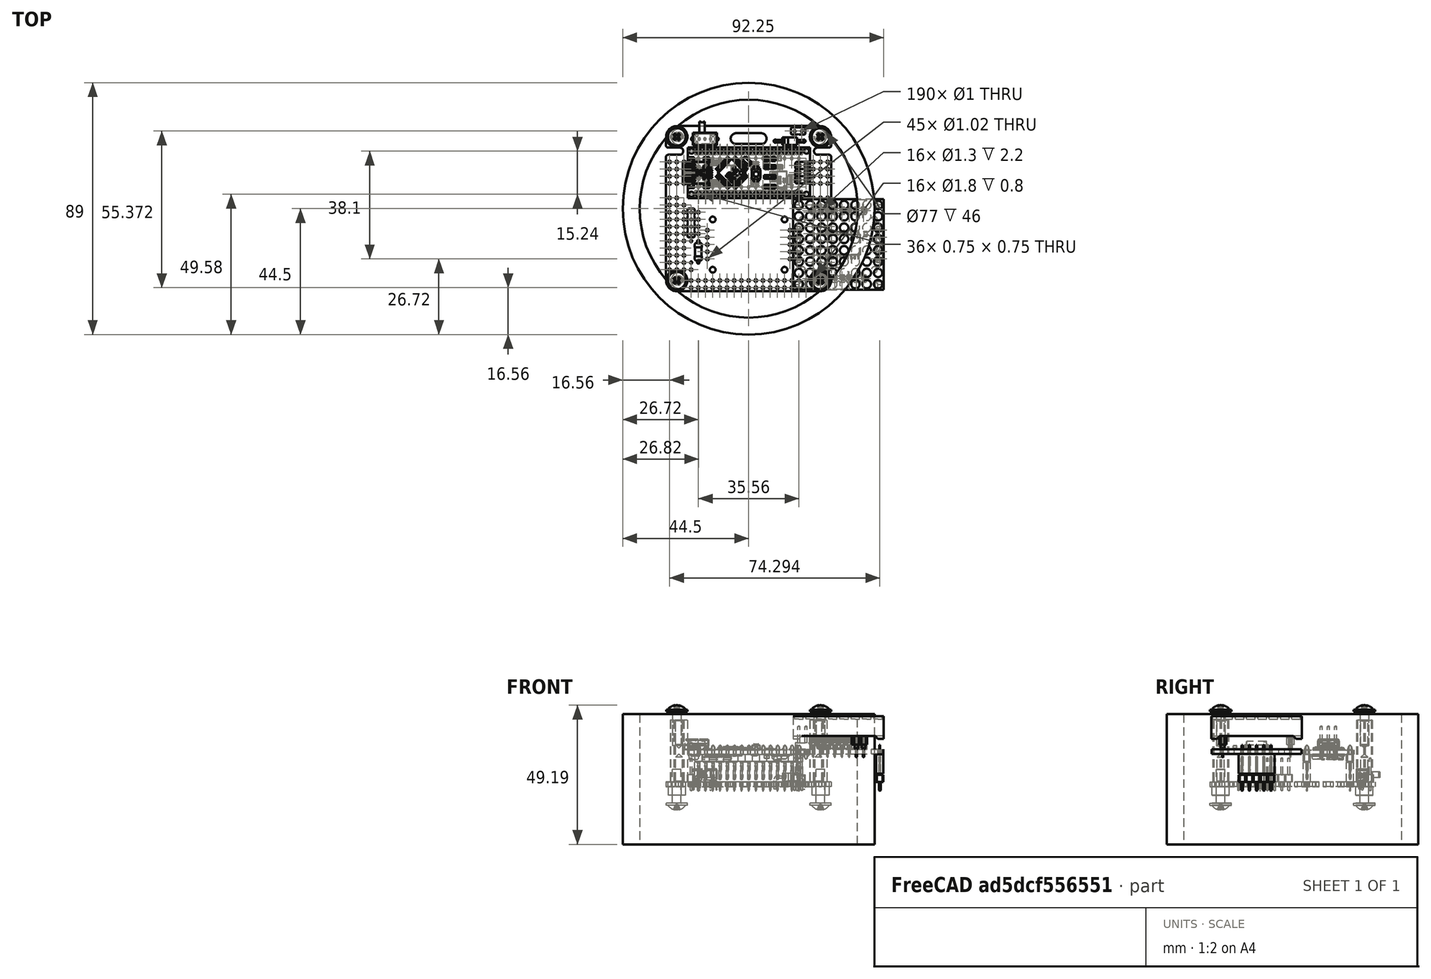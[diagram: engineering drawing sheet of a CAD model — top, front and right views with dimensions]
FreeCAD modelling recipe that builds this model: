
FCSTD DOCUMENT  (FreeCAD 2023.521R14555 (Git shallow))
Label: BagTag_v31
License: All rights reserved
LicenseURL: http://en.wikipedia.org/wiki/All_rights_reserved
objects: Part::Feature×22, Part::FeaturePython×12, App::DocumentObjectGroupPython×8, PartDesign::Body×7, Sketcher::SketchObject×5, PartDesign::SubShapeBinder×5, App::Part×5, PartDesign::Pad×4, App::DocumentObjectGroup×3, App::Link×3, Part::Part2DObjectPython×3, PartDesign::FeatureBase×3, PartDesign::CoordinateSystem×1, PartDesign::ShapeBinder×1, Part::SubShapeBinder×1
note: 80 computed .brp shape members not serialized (recipe doc carries the construction recipe); baked Part::Feature solids carry a one-line shape summary decoded from their .brp

FEATURE [Sketcher::SketchObject] Sketch
  ArcFitTolerance = 0
  AttachmentSupport = -> [XY_Plane011]
  ExternalBSplineMaxDegree = 0
  ExternalBSplineTolerance = 0
  FullyConstrained = true
  InternalTolerance = 1e-06
  InvalidShape = false
  MakeInternals = false
  MapMode = 5
  Support = -> [XY_Plane011]
  TreeRank = 0
  ValidateShape = false
  sketch-geometry (2):
    g0: Circle CenterX=0 CenterY=0 CenterZ=0 NormalX=0 NormalY=0 NormalZ=1 AngleXU=0 Radius=38.5
    g1: Circle CenterX=0 CenterY=0 CenterZ=0 NormalX=0 NormalY=0 NormalZ=1 AngleXU=0 Radius=44.5
  constraints (4):
    c: Coincident(g0,g-1)
    c: Diameter(g0) = 77
    c: Diameter(g1) = 89
    c: Coincident(g1,g0)
FEATURE [PartDesign::Pad] Pad
  AddSubType = 0
  AutoTaperInnerAngle = false
  CheckUpToFaceLimits = true
  ClaimChildren = false
  Direction = (0,0,1)
  Fit = 0
  FitJoin = 0
  InnerFit = 0
  InnerFitJoin = 0
  InvalidShape = false
  Length = 24
  Length2 = 22
  NewSolid = false
  Profile = -> Sketch
  Suppress = false
  TaperInnerAngle = 0
  TaperInnerAngleRev = 0
  TreeRank = 0
  Type = 4
  ValidateShape = true
  _ProfileBasedVersion = 0
FEATURE [PartDesign::Body] Body  label="PVC_pipe"
  AutoGroupSolids = false
  ClaimAllChildren = false
  ExportMode = 0
  Group = -> [Sketch,Pad]
  InvalidShape = false
  Origin = -> Origin011
  Tip = -> Pad
  TreeRank = 0
  ValidateShape = false
  _ExportChildren = -> [Pad]
  _GroupVersion = 1
FEATURE [Part::FeaturePython] Spacer  label="M3x22xx5.5-Spacer168"  # Fasteners workbench fastener (typed FeaturePython)
  InvalidShape = false
  Placement = pos=(-24.638,-25.4,0) rot=(0,0,1;0rad)
  TreeRank = 0
  ValidateShape = false
  diameter = 2
  invert = false
  leftHanded = false
  length = 17
  lengthCustom = 22
  matchOuter = false
  offset = 0
  thread = false
  type = 0
  width = 1
FEATURE [Part::FeaturePython] Spacer001  label="M3x22xx5.5-Spacer169"  # Fasteners workbench fastener (typed FeaturePython)
  InvalidShape = false
  Placement = pos=(24.638,-25.4,0) rot=(0,0,1;0rad)
  TreeRank = 0
  ValidateShape = false
  diameter = 2
  invert = false
  leftHanded = false
  length = 17
  lengthCustom = 22
  matchOuter = false
  offset = 0
  thread = false
  type = 0
  width = 1
FEATURE [Part::FeaturePython] Spacer002  label="M3x22xx5.5-Spacer"  # Fasteners workbench fastener (typed FeaturePython)
  InvalidShape = false
  Placement = pos=(-24.638,25.4,0) rot=(0,0,1;0rad)
  TreeRank = 0
  ValidateShape = false
  diameter = 2
  invert = false
  leftHanded = false
  length = 17
  lengthCustom = 22
  matchOuter = false
  offset = 0
  thread = false
  type = 0
  width = 1
FEATURE [Part::FeaturePython] Spacer003  label="M3x22xx5.5-Spacer170"  # Fasteners workbench fastener (typed FeaturePython)
  InvalidShape = false
  Placement = pos=(24.638,25.4,0) rot=(0,0,1;0rad)
  TreeRank = 0
  ValidateShape = false
  diameter = 2
  invert = false
  leftHanded = false
  length = 17
  lengthCustom = 22
  matchOuter = false
  offset = 0
  thread = false
  type = 0
  width = 1
FEATURE [Part::FeaturePython] Screw  label="M3x12-Screw"  # Fasteners workbench fastener (typed FeaturePython)
  InvalidShape = false
  Placement = pos=(-25.4,25.4,-7.5) rot=(-1,0,0;3.14159rad)
  TreeRank = 0
  ValidateShape = false
  baseObject = -> Body001 [Edge48]
  diameter = 1
  invert = true
  leftHanded = false
  length = 5
  lengthCustom = 12
  matchOuter = false
  offset = 0
  thread = false
  type = 22
FEATURE [Part::FeaturePython] Screw001  label="M3x12-Screw529"  # Fasteners workbench fastener (typed FeaturePython)
  InvalidShape = false
  Placement = pos=(25.4,25.4,-7.5) rot=(-1,0,0;3.14159rad)
  TreeRank = 0
  ValidateShape = false
  baseObject = -> Body001 [Edge45]
  diameter = 1
  invert = true
  leftHanded = false
  length = 5
  lengthCustom = 12
  matchOuter = false
  offset = 0
  thread = false
  type = 22
FEATURE [Part::FeaturePython] Screw002  label="M3x12-Screw530"  # Fasteners workbench fastener (typed FeaturePython)
  InvalidShape = false
  Placement = pos=(-25.4,-25.4,-7.5) rot=(-1,0,0;3.14159rad)
  TreeRank = 0
  ValidateShape = false
  baseObject = -> Body001 [Edge51]
  diameter = 1
  invert = true
  leftHanded = false
  length = 5
  lengthCustom = 12
  matchOuter = false
  offset = 0
  thread = false
  type = 22
FEATURE [Part::FeaturePython] Screw003  label="M3x12-Screw531"  # Fasteners workbench fastener (typed FeaturePython)
  InvalidShape = false
  Placement = pos=(25.4,-25.4,-7.5) rot=(-1,0,0;3.14159rad)
  TreeRank = 0
  ValidateShape = false
  baseObject = -> Body001 [Edge54]
  diameter = 1
  invert = true
  leftHanded = false
  length = 5
  lengthCustom = 12
  matchOuter = false
  offset = 0
  thread = false
  type = 22
FEATURE [PartDesign::SubShapeBinder] Binder003
  BindCopyOnChange = 0
  BindMode = 0
  ClaimChildren = false
  Context = -> Body003 [Binder003.]
  EdgeTolerance = 1e-06
  FillStyle = 0
  Fuse = false
  InvalidShape = false
  MakeFace = true
  MergeEdges = true
  OffsetFill = false
  OffsetIntersection = false
  OffsetJoinType = 0
  OffsetOpenResult = false
  Outline = false
  PartialLoad = false
  Relative = true
  SplitEdges = false
  Support = -> [Body001]
  TightBound = false
  TreeRank = 0
  ValidateShape = false
  _Version = 2
FEATURE [Part::FeaturePython] Screw004  label="M3x12-Screw692"  # Fasteners workbench fastener (typed FeaturePython)
  InvalidShape = false
  Placement = pos=(-25.4,25.4,24.9) rot=(0,0,1;0rad)
  TreeRank = 0
  ValidateShape = false
  baseObject = -> Body003 [Edge96]
  diameter = 1
  invert = false
  leftHanded = false
  length = 5
  lengthCustom = 12
  matchOuter = false
  offset = 0
  thread = false
  type = 22
FEATURE [Part::FeaturePython] Screw005  label="M3x12-Screw693"  # Fasteners workbench fastener (typed FeaturePython)
  InvalidShape = false
  Placement = pos=(25.4,25.4,24.9) rot=(0,0,1;0rad)
  TreeRank = 0
  ValidateShape = false
  baseObject = -> Body003 [Edge93]
  diameter = 1
  invert = false
  leftHanded = false
  length = 5
  lengthCustom = 12
  matchOuter = false
  offset = 0
  thread = false
  type = 22
FEATURE [Part::FeaturePython] Screw006  label="M3x12-Screw694"  # Fasteners workbench fastener (typed FeaturePython)
  InvalidShape = false
  Placement = pos=(-25.4,-25.4,24.9) rot=(0,0,1;0rad)
  TreeRank = 0
  ValidateShape = false
  baseObject = -> Body003 [Edge99]
  diameter = 1
  invert = false
  leftHanded = false
  length = 5
  lengthCustom = 12
  matchOuter = false
  offset = 0
  thread = false
  type = 22
FEATURE [Part::FeaturePython] Screw007  label="M3x12-Screw695"  # Fasteners workbench fastener (typed FeaturePython)
  InvalidShape = false
  Placement = pos=(25.4,-25.4,24.9) rot=(0,0,1;0rad)
  TreeRank = 0
  ValidateShape = false
  baseObject = -> Body003 [Edge102]
  diameter = 1
  invert = false
  leftHanded = false
  length = 5
  lengthCustom = 12
  matchOuter = false
  offset = 0
  thread = false
  type = 22
FEATURE [App::DocumentObjectGroup] Group001  label="Fasteners"
  ClaimAllChildren = true
  ExportMode = 1
  Group = -> [Spacer,Spacer001,Spacer002,Spacer003,Screw,Screw001,Screw002,Screw003,Screw004,Screw005,Screw006,Screw007]
  TreeRank = 0
  _GroupVersion = 1
FEATURE [PartDesign::SubShapeBinder] Binder005  label="Binder005(M3x22xx5.5-Spacer033)"
  BindCopyOnChange = 0
  BindMode = 0
  ClaimChildren = false
  Context = -> Body003 [Binder005.]
  EdgeTolerance = 1e-06
  FillStyle = 0
  Fuse = false
  InvalidShape = false
  MakeFace = true
  MergeEdges = true
  OffsetFill = false
  OffsetIntersection = false
  OffsetJoinType = 0
  OffsetOpenResult = false
  Outline = false
  PartialLoad = false
  Relative = true
  SplitEdges = false
  Support = -> [Spacer]
  TightBound = false
  TreeRank = 1
  ValidateShape = false
  _Version = 8
FEATURE [Part::Feature] Compound  label="pp3_battery"
  InvalidShape = false
  Placement = pos=(2.6,-25,8.6) rot=(1,0,0;1.5708rad)
  TreeRank = 36
  ValidateShape = false
  shape: bbox 46.52 x 16.6 x 26 mm, 243 faces, 0 solids (baked)
FEATURE [Part::Feature] trajectory_line
  InvalidShape = false
  TreeRank = 545
  ValidateShape = false
  shape: bbox 49.28 x 50.8 x 150 mm, 0 faces, 0 solids (baked)
FEATURE [App::DocumentObjectGroupPython] BoltGroup  # scripted group (container) (typed FeaturePython)
  AnimationStepTime = 0.1
  AnimationSteps = 20
  ClaimAllChildren = true
  Distance = 150
  ExportMode = 0
  Group = -> [trajectory_line]
  Revolutions = 0
  TreeRank = 5
  _GroupVersion = 1
FEATURE [Part::Feature] trajectory_line001
  InvalidShape = false
  TreeRank = 546
  ValidateShape = false
  shape: bbox 2e-07 x 2e-07 x 140 mm, 0 faces, 0 solids (baked)
FEATURE [App::DocumentObjectGroupPython] SimpleGroup  # scripted group (container) (typed FeaturePython)
  AnimationStepTime = 0.05
  AnimationSteps = 20
  ClaimAllChildren = true
  Distance = 140
  ExportMode = 0
  Group = -> [trajectory_line001]
  Revolutions = 0
  TreeRank = 9
  _GroupVersion = 1
FEATURE [Part::Feature] trajectory_line002
  InvalidShape = false
  TreeRank = 547
  ValidateShape = false
  shape: bbox 49.28 x 50.8 x 120 mm, 0 faces, 0 solids (baked)
FEATURE [App::DocumentObjectGroupPython] BoltGroup001  # scripted group (container) (typed FeaturePython)
  AnimationStepTime = 0.05
  AnimationSteps = 20
  ClaimAllChildren = true
  Distance = 120
  ExportMode = 0
  Group = -> [trajectory_line002]
  Revolutions = 0
  TreeRank = 15
  _GroupVersion = 1
FEATURE [Part::Feature] trajectory_line003
  InvalidShape = false
  TreeRank = 548
  ValidateShape = false
  shape: bbox 2e-07 x 100 x 2e-07 mm, 0 faces, 0 solids (baked)
FEATURE [App::DocumentObjectGroupPython] SimpleGroup001  # scripted group (container) (typed FeaturePython)
  AnimationStepTime = 0
  AnimationSteps = 20
  ClaimAllChildren = true
  Distance = 100
  ExportMode = 0
  Group = -> [trajectory_line003]
  Revolutions = 0
  TreeRank = 42
  _GroupVersion = 1
FEATURE [Part::Feature] trajectory_line004
  InvalidShape = false
  TreeRank = 549
  ValidateShape = false
  shape: bbox 2e-07 x 2e-07 x 100 mm, 0 faces, 0 solids (baked)
FEATURE [App::DocumentObjectGroupPython] SimpleGroup002  # scripted group (container) (typed FeaturePython)
  AnimationStepTime = 0
  AnimationSteps = 20
  ClaimAllChildren = true
  Distance = 100
  ExportMode = 0
  Group = -> [trajectory_line004]
  Revolutions = 0
  TreeRank = 518
  _GroupVersion = 1
FEATURE [Part::Feature] trajectory_line005
  InvalidShape = false
  TreeRank = 550
  ValidateShape = false
  shape: bbox 2e-07 x 2e-07 x 80 mm, 0 faces, 0 solids (baked)
FEATURE [App::DocumentObjectGroupPython] BoltGroup002  # scripted group (container) (typed FeaturePython)
  AnimationStepTime = 0
  AnimationSteps = 20
  ClaimAllChildren = true
  Distance = 80
  ExportMode = 0
  Group = -> [trajectory_line005]
  Revolutions = 0
  TreeRank = 530
  _GroupVersion = 1
FEATURE [Part::Feature] trajectory_line006
  InvalidShape = false
  TreeRank = 543
  ValidateShape = false
  shape: bbox 2e-07 x 2e-07 x 20 mm, 0 faces, 0 solids (baked)
FEATURE [App::DocumentObjectGroupPython] SimpleGroup003  # scripted group (container) (typed FeaturePython)
  AnimationStepTime = 0
  AnimationSteps = 20
  ClaimAllChildren = true
  Distance = 50
  ExportMode = 0
  Group = -> [trajectory_line006]
  Revolutions = 0
  TreeRank = 544
  _GroupVersion = 1
FEATURE [App::DocumentObjectGroupPython] ExplodedAssembly  # scripted group (container) (typed FeaturePython)
  AnimationStep = 0
  ClaimAllChildren = true
  CurrentTrajectory = 0
  ExportMode = 0
  Group = -> [BoltGroup,SimpleGroup,BoltGroup001,SimpleGroup001,SimpleGroup002,BoltGroup002,SimpleGroup003]
  InAnimation = false
  RemoveAllTrajectories = false
  ResetAnimation = false
  TreeRank = 2
  _GroupVersion = 1
FEATURE [PartDesign::CoordinateSystem] Local_CS_fc76
  AttacherType = Attacher::AttachEngine3D
  FixShape = 1
  InvalidShape = false
  MapMode = 2
  TreeRank = 596
  ValidateShape = false
FEATURE [Part::Feature] Pcb_fc76
  FixShape = 1
  InvalidShape = false
  Placement = pos=(-80.01,80.01,0) rot=(0,0,1;0rad)
  TreeRank = 597
  ValidateShape = false
  shape: bbox 58.42 x 58.42 x 1.6 mm, 260 faces (baked)
FEATURE [Sketcher::SketchObject] PCB_Sketch_fc76
  ArcFitTolerance = 1e-06
  ExternalBSplineMaxDegree = 5
  ExternalBSplineTolerance = 0.0001
  FixShape = 1
  FullyConstrained = false
  InternalTolerance = 1e-06
  InvalidShape = false
  MakeInternals = false
  TreeRank = 602
  ValidateShape = false
  sketch-geometry (28):
    g0: LineSegment StartX=4.445 StartY=22.86 StartZ=0 EndX=-4.445 EndY=22.86 EndZ=0
    g1: LineSegment StartX=28.448 StartY=21.59 StartZ=0 EndX=24.384 EndY=21.59 EndZ=0
    g2: LineSegment StartX=-29.21 StartY=25.781 StartZ=0 EndX=-25.781 EndY=29.21 EndZ=0
    g3: LineSegment StartX=-25.781 StartY=29.21 StartZ=0 EndX=25.781 EndY=29.21 EndZ=0
    g4: LineSegment StartX=29.21 StartY=25.781 StartZ=0 EndX=25.781 EndY=29.21 EndZ=0
    g5: LineSegment StartX=25.781 StartY=-29.21 StartZ=0 EndX=29.21 EndY=-25.781 EndZ=0
    g6: LineSegment StartX=25.781 StartY=-29.21 StartZ=0 EndX=-25.781 EndY=-29.21 EndZ=0
    g7: LineSegment StartX=-29.21 StartY=-25.781 StartZ=0 EndX=-25.781 EndY=-29.21 EndZ=0
    g8: LineSegment StartX=29.21 StartY=25.781 StartZ=0 EndX=29.21 EndY=22.352 EndZ=0
    g9: LineSegment StartX=29.21 StartY=18.288 StartZ=0 EndX=29.21 EndY=-25.781 EndZ=0
    g10: LineSegment StartX=-24.384 StartY=21.59 StartZ=0 EndX=-28.448 EndY=21.59 EndZ=0
    g11: LineSegment StartX=-28.448 StartY=19.05 StartZ=0 EndX=-24.384 EndY=19.05 EndZ=0
    g12: LineSegment StartX=-4.445 StartY=26.67 StartZ=0 EndX=4.445 EndY=26.67 EndZ=0
    g13: LineSegment StartX=24.384 StartY=19.05 StartZ=0 EndX=28.448 EndY=19.05 EndZ=0
    g14: LineSegment StartX=-29.21 StartY=25.781 StartZ=0 EndX=-29.21 EndY=22.352 EndZ=0
    g15: LineSegment StartX=-29.21 StartY=-25.781 StartZ=0 EndX=-29.21 EndY=18.288 EndZ=0
    g16: ArcOfCircle CenterX=28.448 CenterY=18.288 CenterZ=0 NormalX=0 NormalY=0 NormalZ=-1 AngleXU=1.5708 Radius=0.762001 StartAngle=0 EndAngle=1.57079
    g17: ArcOfCircle CenterX=-4.445 CenterY=24.765 CenterZ=0 NormalX=0 NormalY=0 NormalZ=-1 AngleXU=-1.5708 Radius=1.905 StartAngle=0 EndAngle=3.14159
    g18: ArcOfCircle CenterX=-28.448 CenterY=18.288 CenterZ=0 NormalX=0 NormalY=0 NormalZ=-1 AngleXU=1.64556e-06 Radius=0.762001 StartAngle=0 EndAngle=1.57079
    g19: ArcOfCircle CenterX=-28.448 CenterY=22.352 CenterZ=0 NormalX=0 NormalY=0 NormalZ=-1 AngleXU=-1.57079 Radius=0.762001 StartAngle=0 EndAngle=1.57079
    g20: ArcOfCircle CenterX=-24.384 CenterY=20.32 CenterZ=0 NormalX=0 NormalY=0 NormalZ=-1 AngleXU=1.5708 Radius=1.27 StartAngle=0 EndAngle=3.14159
    g21: ArcOfCircle CenterX=4.445 CenterY=24.765 CenterZ=0 NormalX=0 NormalY=0 NormalZ=-1 AngleXU=1.5708 Radius=1.905 StartAngle=0 EndAngle=3.14159
    g22: ArcOfCircle CenterX=24.384 CenterY=20.32 CenterZ=0 NormalX=0 NormalY=0 NormalZ=-1 AngleXU=-1.5708 Radius=1.27 StartAngle=0 EndAngle=3.14159
    g23: ArcOfCircle CenterX=28.448 CenterY=22.352 CenterZ=0 NormalX=0 NormalY=0 NormalZ=-1 AngleXU=-3.14159 Radius=0.762001 StartAngle=0 EndAngle=1.57079
    g24: Circle CenterX=25.4 CenterY=25.4 CenterZ=0 NormalX=0 NormalY=0 NormalZ=1 AngleXU=0 Radius=1.524
    g25: Circle CenterX=-25.4 CenterY=-25.4 CenterZ=0 NormalX=0 NormalY=0 NormalZ=1 AngleXU=0 Radius=1.524
    g26: Circle CenterX=25.4 CenterY=-25.4 CenterZ=0 NormalX=0 NormalY=0 NormalZ=1 AngleXU=0 Radius=1.524
    g27: Circle CenterX=-25.4 CenterY=25.4 CenterZ=0 NormalX=0 NormalY=0 NormalZ=1 AngleXU=0 Radius=1.524
  constraints (24):
    c: Coincident(g7,g15)
    c: Coincident(g15,g18)
    c: Coincident(g14,g19)
    c: Coincident(g2,g14)
    c: Coincident(g11,g18)
    c: Coincident(g10,g19)
    c: Coincident(g6,g7)
    c: Coincident(g2,g3)
    c: Coincident(g11,g20)
    c: Coincident(g10,g20)
    c: Coincident(g0,g17)
    c: Coincident(g12,g17)
    c: Coincident(g0,g21)
    c: Coincident(g12,g21)
    c: Coincident(g13,g22)
    c: Coincident(g1,g22)
    c: Coincident(g5,g6)
    c: Coincident(g3,g4)
    c: Coincident(g13,g16)
    c: Coincident(g1,g23)
    c: Coincident(g5,g9)
    c: Coincident(g9,g16)
    c: Coincident(g8,g23)
    c: Coincident(g4,g8)
FEATURE [App::Part] Bot_fc76
  ClaimAllChildren = false
  ExportMode = 1
  Origin = -> Origin028
  TreeRank = 608
  _GroupVersion = 1
FEATURE [Part::Feature] Shape001  label="LED2_FC_16_cp_sp_3f0951532924"
  FixShape = 1
  InvalidShape = false
  Placement = pos=(31.75,-12.7,0) rot=(0,0,1;0rad)
  TreeRank = 685
  ValidateShape = false
  shape: bbox 32 x 32 x 26.3 mm, 2206 faces, 44 solids (baked)
FEATURE [Part::Feature] Shape002  label="BT1_PinHeader_1x02_P254mm_Vertical_64228b7c207f"
  FixShape = 1
  InvalidShape = false
  Placement = pos=(16.246,27.432,0) rot=(0,0,1;1.5708rad)
  TreeRank = 705
  ValidateShape = false
  shape: bbox 5.08 x 2.54 x 11.54 mm, 52 faces (baked)
FEATURE [Part::Feature] Shape004  label="J2_PinHeader_1x04_P254mm_Vertical_b8c18ff84878"
  FixShape = 1
  InvalidShape = false
  Placement = pos=(-20.32,-1.27,0) rot=(0,0,1;0rad)
  TreeRank = 733
  ValidateShape = false
  shape: bbox 2.54 x 10.16 x 11.54 mm, 100 faces (baked)
FEATURE [App::Link] LED2_FC_16_cp_sp_3f0951532924_ln_  label="LED1_FC_16_cp_sp_494d2cd2c793"
  AutoLinkLabel = true
  AutoPlacement = true
  LinkPlacement = pos=(0,-12.7,0) rot=(0,0,1;0rad)
  LinkedObject = -> Shape001
  Placement = pos=(0,-12.7,0) rot=(0,0,1;0rad)
  SyncGroupVisibility = false
  TreeRank = 735
  _LinkVersion = 1
FEATURE [App::Link] J2_PinHeader_1x04_P254mm_Vertical_b8c18ff84878_ln_  label="J1_PinHeader_1x04_P254mm_Vertical_d596b9d5dcda"
  AutoLinkLabel = true
  AutoPlacement = true
  LinkPlacement = pos=(-17.78,-1.27,0) rot=(0,0,1;0rad)
  LinkedObject = -> Shape004
  Placement = pos=(-17.78,-1.27,0) rot=(0,0,1;0rad)
  SyncGroupVisibility = false
  TreeRank = 761
  _LinkVersion = 1
FEATURE [Part::Feature] Shape005  label="R2_R_Axial_DIN0207_L63mm_D25mm_P762mm_Horizontal_4ffd937b06bc"
  FixShape = 1
  InvalidShape = false
  Placement = pos=(-17.78,-19.05,0) rot=(0,0,1;1.5708rad)
  TreeRank = 805
  ValidateShape = false
  shape: bbox 2.706 x 8.418 x 5.603 mm, 15 faces (baked)
FEATURE [Part::Feature] Shape006  label="U1_arduino_nano_socket_d5ff97aaa247"
  FixShape = 1
  InvalidShape = false
  Placement = pos=(20.32,12.7,0) rot=(0,0,-1;1.5708rad)
  TreeRank = 837
  ValidateShape = false
  shape: bbox 45 x 18 x 22.97 mm, 7207 faces, 57 solids (baked)
FEATURE [Part::Feature] Shape007  label="SW1_1_219a87e7a09f"
  FixShape = 1
  InvalidShape = false
  Placement = pos=(-13.462,24.638,0) rot=(0,0,1;3.14159rad)
  TreeRank = 855
  ValidateShape = false
  shape: bbox 8.6 x 8.4 x 7.6 mm, 200 faces (baked)
FEATURE [Part::Feature] Shape008  label="D1_D_DO-41_SOD81_P10.16mm_Horizontal_32ec51f60e8f"
  FixShape = 1
  InvalidShape = false
  Placement = pos=(9.398,23.876,0) rot=(0,0,1;0rad)
  TreeRank = 892
  ValidateShape = false
  shape: bbox 11.16 x 2.72 x 5.71 mm, 15 faces (baked)
FEATURE [App::Link] R2_R_Axial_DIN0207_L63mm_D25mm_P762mm_Horizontal_4ffd937b06bc_ln_  label="R1_R_Axial_DIN0207_L63mm_D25mm_P762mm_Horizontal_6afa1d7f9f45"
  AutoLinkLabel = true
  AutoPlacement = true
  LinkPlacement = pos=(-20.32,-19.05,0) rot=(0,0,1;1.5708rad)
  LinkedObject = -> Shape005
  Placement = pos=(-20.32,-19.05,0) rot=(0,0,1;1.5708rad)
  SyncGroupVisibility = false
  TreeRank = 894
  _LinkVersion = 1
FEATURE [App::Part] Top_fc76
  ClaimAllChildren = false
  ExportMode = 1
  Group = -> [Shape001,Shape002,Shape004,LED2_FC_16_cp_sp_3f0951532924_ln_,J2_PinHeader_1x04_P254mm_Vertical_b8c18ff84878_ln_,Shape005,Shape006,Shape007,Shape008,R2_R_Axial_DIN0207_L63mm_D25mm_P762mm_Horizontal_4ffd937b06bc_ln_]
  Origin = -> Origin027
  TreeRank = 606
  _ExportChildren = -> [Shape001,Shape002,Shape004,LED2_FC_16_cp_sp_3f0951532924_ln_,J2_PinHeader_1x04_P254mm_Vertical_b8c18ff84878_ln_,Shape005,Shape006,Shape007,Shape008,R2_R_Axial_DIN0207_L63mm_D25mm_P762mm_Horizontal_4ffd937b06bc_ln_]
  _GroupVersion = 1
FEATURE [App::Part] Step_Models_fc76
  ClaimAllChildren = false
  ExportMode = 1
  Group = -> [Top_fc76,Bot_fc76]
  Origin = -> Origin026
  TreeRank = 604
  _ExportChildren = -> [Top_fc76,Bot_fc76]
  _GroupVersion = 1
FEATURE [Part::Feature] pads_area001  label="topPads_fc76"
  FixShape = 1
  InvalidShape = false
  Placement = pos=(-80.01,80.01,0.02) rot=(0,0,1;0rad)
  TreeRank = 2449
  ValidateShape = false
  shape: bbox 57.58 x 57.07 x 2e-07 mm, 226 faces, 0 solids (baked)
FEATURE [Part::Feature] Shape009  label="topTracks_fc76"
  FixShape = 1
  InvalidShape = false
  Placement = pos=(-80.01,80.01,0.01) rot=(0,0,1;0rad)
  TreeRank = 2479
  ValidateShape = false
  shape: bbox 50.8 x 47.75 x 2e-07 mm, 60 faces, 0 solids (baked)
FEATURE [Part::Feature] pads_area002001  label="botPads_fc76"
  FixShape = 1
  InvalidShape = false
  Placement = pos=(-80.01,80.01,-1.62) rot=(0,0,1;0rad)
  TreeRank = 3882
  ValidateShape = false
  shape: bbox 57.58 x 57.07 x 2e-07 mm, 226 faces, 0 solids (baked)
FEATURE [Part::Feature] Shape010001  label="botTracks_fc76"
  FixShape = 1
  InvalidShape = false
  Placement = pos=(-80.01,80.01,-1.61) rot=(0,0,1;0rad)
  TreeRank = 3912
  ValidateShape = false
  shape: bbox 49.91 x 45.04 x 2e-07 mm, 36 faces, 0 solids (baked)
FEATURE [Part::Feature] zones_area001  label="botZones_fc76"
  FixShape = 1
  InvalidShape = false
  Placement = pos=(-80.01,80.01,-1.61) rot=(0,0,1;0rad)
  TreeRank = 4046
  ValidateShape = false
  shape: bbox 58.47 x 58.47 x 2e-07 mm, 21 faces, 0 solids (baked)
FEATURE [Part::Feature] topSilks_ac4f
  FixShape = 1
  InvalidShape = false
  Placement = pos=(-80.01,80.01,0.07) rot=(0,0,1;0rad)
  TreeRank = 4416
  ValidateShape = false
  shape: bbox 58.06 x 57.85 x 2e-07 mm, 363 faces, 0 solids (baked)
FEATURE [App::Part] Board_Geoms_fc76
  ClaimAllChildren = false
  ExportMode = 1
  Group = -> [Pcb_fc76,PCB_Sketch_fc76,pads_area001,Shape009,pads_area002001,Shape010001,zones_area001,topSilks_ac4f]
  Origin = -> Origin
  TreeRank = 599
  _ExportChildren = -> [Pcb_fc76,PCB_Sketch_fc76,pads_area001,Shape009,pads_area002001,Shape010001,zones_area001,topSilks_ac4f]
  _GroupVersion = 1
FEATURE [App::Part] Board_fc76  label="BagTag"
  ClaimAllChildren = false
  ExportMode = 1
  Group = -> [Local_CS_fc76,Board_Geoms_fc76,Step_Models_fc76]
  Origin = -> Origin025
  TreeRank = 601
  _ExportChildren = -> [Local_CS_fc76,Board_Geoms_fc76,Step_Models_fc76]
  _GroupVersion = 1
FEATURE [PartDesign::ShapeBinder] ShapeBinder
  FixShape = 1
  InvalidShape = false
  Placement = pos=(-80.01,80.01,0) rot=(0,0,1;0rad)
  Support = -> [Pcb_fc76]
  TraceSupport = false
  TreeRank = 4417
  ValidateShape = false
FEATURE [Part::SubShapeBinder] Import  label="Import(Pcb_fc76)"
  BindCopyOnChange = 0
  BindMode = 0
  ClaimChildren = false
  Context = -> Body001 [Import.]
  EdgeTolerance = 1e-06
  FillStyle = 0
  FixShape = 1
  Fuse = false
  InvalidShape = false
  MakeFace = false
  MergeEdges = true
  OffsetFill = false
  OffsetIntersection = false
  OffsetJoinType = 0
  OffsetOpenResult = false
  Outline = false
  PartialLoad = false
  Relative = true
  SplitEdges = false
  Support = -> [Board_fc76[Board_Geoms_fc76.Pcb_fc76.]]
  TightBound = false
  TreeRank = 4418
  ValidateShape = false
  _Version = 8
FEATURE [Sketcher::SketchObject] Sketch001
  ArcFitTolerance = 0
  AttachmentSupport = -> [XY_Plane020]
  ExternalBSplineMaxDegree = 0
  ExternalBSplineTolerance = 0
  ExternalGeometry = -> [Import]
  FullyConstrained = true
  InternalTolerance = 1e-06
  InvalidShape = false
  MakeInternals = false
  MapMode = 5
  Support = -> [XY_Plane020]
  TreeRank = 0
  ValidateShape = false
  sketch-geometry (22):
    g0: LineSegment StartX=-25.4 StartY=29.9 StartZ=0 EndX=25.4 EndY=29.9 EndZ=0
    g1: LineSegment StartX=29.9 StartY=25.4 StartZ=0 EndX=29.9 EndY=-41.6 EndZ=0
    g2: LineSegment StartX=25.4 StartY=-46.1 StartZ=0 EndX=-25.4 EndY=-46.1 EndZ=0
    g3: LineSegment StartX=-29.9 StartY=-41.6 StartZ=0 EndX=-29.9 EndY=25.4 EndZ=0
    g4: ArcOfCircle CenterX=-25.4 CenterY=25.4 CenterZ=0 NormalX=0 NormalY=0 NormalZ=1 AngleXU=0 Radius=4.5 StartAngle=1.5708 EndAngle=3.14159
    g5: GeomPoint [constr] X=-29.9 Y=29.9 Z=0
    g6: ArcOfCircle CenterX=25.4 CenterY=25.4 CenterZ=0 NormalX=0 NormalY=0 NormalZ=1 AngleXU=0 Radius=4.5 StartAngle=0 EndAngle=1.5708
    g7: GeomPoint [constr] X=29.9 Y=29.9 Z=0
    g8: ArcOfCircle CenterX=25.4 CenterY=-41.6 CenterZ=0 NormalX=0 NormalY=0 NormalZ=1 AngleXU=0 Radius=4.5 StartAngle=4.71239 EndAngle=6.28319
    g9: GeomPoint [constr] X=29.9 Y=-46.1 Z=0
    g10: ArcOfCircle CenterX=-25.4 CenterY=-41.6 CenterZ=0 NormalX=0 NormalY=0 NormalZ=1 AngleXU=0 Radius=4.5 StartAngle=3.14159 EndAngle=4.71239
    g11: GeomPoint [constr] X=-29.9 Y=-46.1 Z=0
    g12: Circle CenterX=-25.4 CenterY=-41.6 CenterZ=0 NormalX=0 NormalY=0 NormalZ=1 AngleXU=0 Radius=1.525
    g13: Circle CenterX=25.4 CenterY=-41.6 CenterZ=0 NormalX=0 NormalY=0 NormalZ=1 AngleXU=0 Radius=1.525
    g14: Circle CenterX=25.4 CenterY=25.4 CenterZ=0 NormalX=0 NormalY=0 NormalZ=1 AngleXU=0 Radius=1.525
    g15: Circle CenterX=-25.4 CenterY=25.4 CenterZ=0 NormalX=0 NormalY=0 NormalZ=1 AngleXU=0 Radius=1.525
    g16: ArcOfCircle CenterX=-4.445 CenterY=24.765 CenterZ=0 NormalX=0 NormalY=0 NormalZ=1 AngleXU=0 Radius=1.905 StartAngle=1.5708 EndAngle=4.71239
    g17: ArcOfCircle CenterX=4.445 CenterY=24.765 CenterZ=0 NormalX=0 NormalY=0 NormalZ=1 AngleXU=0 Radius=1.905 StartAngle=4.71239 EndAngle=7.85398
    g18: LineSegment StartX=-4.445 StartY=22.86 StartZ=0 EndX=4.445 EndY=22.86 EndZ=0
    g19: LineSegment StartX=-4.445 StartY=26.67 StartZ=0 EndX=4.445 EndY=26.67 EndZ=0
    g20: Circle CenterX=-25.4 CenterY=-25.4 CenterZ=0 NormalX=0 NormalY=0 NormalZ=1 AngleXU=0 Radius=1.525
    g21: Circle CenterX=25.4 CenterY=-25.4 CenterZ=0 NormalX=0 NormalY=0 NormalZ=1 AngleXU=0 Radius=1.525
  constraints (46):
    c: Horizontal(g0)
    c: Horizontal(g2)
    c: Vertical(g1)
    c: Vertical(g3)
    c: PointOnObject(g5,g0)
    c: PointOnObject(g5,g3)
    c: Tangent(g0,g4) = 1.5708
    c: Tangent(g3,g4) = 1.5708
    c: PointOnObject(g7,g0)
    c: PointOnObject(g7,g1)
    c: Tangent(g0,g6) = 1.5708
    c: Tangent(g1,g6) = 1.5708
    c: PointOnObject(g9,g1)
    c: PointOnObject(g9,g2)
    c: Tangent(g1,g8) = 1.5708
    c: Tangent(g2,g8) = 1.5708
    c: PointOnObject(g11,g3)
    c: PointOnObject(g11,g2)
    c: Tangent(g3,g10) = 1.5708
    c: Tangent(g2,g10) = 1.5708
    c: Equal(g10,g8)
    c: Equal(g8,g6)
    c: Coincident(g12,g10)
    c: Coincident(g13,g8)
    c: Coincident(g14,g6)
    c: Coincident(g15,g4)
    c: Equal(g15,g14)
    c: Equal(g14,g13)
    c: Equal(g13,g12)
    c: Tangent(g16,g19) = 1.5708
    c: Tangent(g16,g18) = -1.5708
    c: Tangent(g18,g17) = -1.5708
    c: Tangent(g19,g17) = 1.5708
    c: Horizontal(g18)
    c: Equal(g20,g15)
    c: Diameter(g15) = 3.05
    c: Equal(g21,g15)
    c: DistanceY(g2,g0) = 76
    c: Coincident(g16,g-7)
    c: Coincident(g17,g-8)
    c: Equal(g17,g-8)
    c: Coincident(g4,g-3)
    c: Coincident(g6,g-4)
    c: Coincident(g20,g-6)
    c: Coincident(g21,g-5)
    c: Radius(g4) = 4.5
FEATURE [PartDesign::Pad] Pad001
  AddSubType = 0
  AutoTaperInnerAngle = false
  CheckUpToFaceLimits = true
  ClaimChildren = false
  Direction = (0,0,1)
  Fit = 0
  FitJoin = 0
  InnerFit = 0
  InnerFitJoin = 0
  InvalidShape = false
  Length = 3
  Length2 = 100
  NewSolid = false
  Profile = -> Sketch001
  Reversed = true
  Suppress = false
  TaperInnerAngle = 0
  TaperInnerAngleRev = 0
  TreeRank = 0
  Type = 0
  ValidateShape = true
  _ProfileBasedVersion = 0
FEATURE [PartDesign::Body] Body001  label="Plate_bottom"
  AutoGroupSolids = false
  ClaimAllChildren = false
  ExportMode = 0
  Group = -> [Sketch001,Pad001,ShapeBinder,Import]
  InvalidShape = false
  Origin = -> Origin020
  Placement = pos=(0,0,-4.5) rot=(0,0,1;0rad)
  Tip = -> Pad001
  TreeRank = 0
  ValidateShape = false
  _ExportChildren = -> [Pad001,ShapeBinder,Import]
  _GroupVersion = 1
FEATURE [Part::Part2DObjectPython] Shape2DView  # Draft 2D object (typed FeaturePython)
  AutoUpdate = true
  Base = -> Body001
  Clip = false
  FuseArch = false
  HiddenLines = false
  InPlace = true
  InvalidShape = false
  OnlySolids = false
  Projection = (0,0,1)
  ProjectionMode = 0
  SegmentLength = 0.05
  Tessellation = false
  TreeRank = 551
  ValidateShape = false
  VisibleOnly = false
FEATURE [PartDesign::SubShapeBinder] Binder006  label="Binder006(LED1_FC_16_cp_sp_494d2cd2c793)"
  BindCopyOnChange = 0
  BindMode = 0
  ClaimChildren = false
  Context = -> Body003 [Binder006.]
  EdgeTolerance = 1e-06
  FillStyle = 0
  FixShape = 1
  Fuse = false
  InvalidShape = false
  MakeFace = true
  MergeEdges = true
  OffsetFill = false
  OffsetIntersection = false
  OffsetJoinType = 0
  OffsetOpenResult = false
  Outline = false
  PartialLoad = false
  Relative = true
  SplitEdges = false
  Support = -> [Board_fc76[Step_Models_fc76.Top_fc76.LED2_FC_16_cp_sp_3f0951532924_ln_.]]
  TightBound = false
  TreeRank = 4419
  ValidateShape = false
  _Version = 8
FEATURE [PartDesign::SubShapeBinder] Binder007  label="Binder007(U1_arduino_nano_socket_d5ff97aaa247)"
  BindCopyOnChange = 0
  BindMode = 0
  ClaimChildren = false
  Context = -> Body003 [Binder007.]
  EdgeTolerance = 1e-06
  FillStyle = 0
  FixShape = 1
  Fuse = false
  InvalidShape = false
  MakeFace = true
  MergeEdges = true
  OffsetFill = false
  OffsetIntersection = false
  OffsetJoinType = 0
  OffsetOpenResult = false
  Outline = false
  PartialLoad = false
  Relative = true
  SplitEdges = false
  Support = -> [Board_fc76[Step_Models_fc76.Top_fc76.Shape006.]]
  TightBound = false
  TreeRank = 4420
  ValidateShape = false
  _Version = 8
FEATURE [Sketcher::SketchObject] Sketch003
  ArcFitTolerance = 0
  AttachmentSupport = -> [Binder005]
  ExternalBSplineMaxDegree = 0
  ExternalBSplineTolerance = 0
  ExternalGeometry = -> [Binder003,Binder006,Binder007]
  FullyConstrained = true
  InternalTolerance = 1e-06
  InvalidShape = false
  MakeInternals = false
  MapMode = 5
  Placement = pos=(0,0,21.3) rot=(0,0,1;0rad)
  Support = -> [Binder005]
  TreeRank = 0
  ValidateShape = false
  sketch-geometry (42):
    g0: LineSegment StartX=-25.4 StartY=29.9 StartZ=0 EndX=25.4 EndY=29.9 EndZ=0
    g1: LineSegment StartX=29.9 StartY=25.4 StartZ=0 EndX=29.9 EndY=-41.6 EndZ=0
    g2: LineSegment StartX=25.4 StartY=-46.1 StartZ=0 EndX=-25.4 EndY=-46.1 EndZ=0
    g3: LineSegment StartX=-29.9 StartY=-41.6 StartZ=0 EndX=-29.9 EndY=25.4 EndZ=0
    g4: ArcOfCircle CenterX=-25.4 CenterY=25.4 CenterZ=0 NormalX=0 NormalY=0 NormalZ=1 AngleXU=0 Radius=4.5 StartAngle=1.5708 EndAngle=3.14159
    g5: GeomPoint [constr] X=-29.9 Y=29.9 Z=0
    g6: ArcOfCircle CenterX=25.4 CenterY=25.4 CenterZ=0 NormalX=0 NormalY=0 NormalZ=1 AngleXU=0 Radius=4.5 StartAngle=-9e-16 EndAngle=1.5708
    g7: GeomPoint [constr] X=29.9 Y=29.9 Z=0
    g8: ArcOfCircle CenterX=25.4 CenterY=-41.6 CenterZ=0 NormalX=0 NormalY=0 NormalZ=1 AngleXU=0 Radius=4.5 StartAngle=4.71239 EndAngle=6.28319
    g9: GeomPoint [constr] X=29.9 Y=-46.1 Z=0
    g10: ArcOfCircle CenterX=-25.4 CenterY=-41.6 CenterZ=0 NormalX=0 NormalY=0 NormalZ=1 AngleXU=0 Radius=4.5 StartAngle=3.14159 EndAngle=4.71239
    g11: GeomPoint [constr] X=-29.9 Y=-46.1 Z=0
    g12: Circle CenterX=-25.4 CenterY=-41.6 CenterZ=0 NormalX=0 NormalY=0 NormalZ=1 AngleXU=0 Radius=1.525
    g13: Circle CenterX=25.4 CenterY=-41.6 CenterZ=0 NormalX=0 NormalY=0 NormalZ=1 AngleXU=0 Radius=1.525
    g14: Circle CenterX=25.4 CenterY=25.4 CenterZ=0 NormalX=0 NormalY=0 NormalZ=1 AngleXU=0 Radius=1.525
    g15: Circle CenterX=-25.4 CenterY=25.4 CenterZ=0 NormalX=0 NormalY=0 NormalZ=1 AngleXU=0 Radius=1.525
    g16: ArcOfCircle CenterX=-4.445 CenterY=24.765 CenterZ=0 NormalX=0 NormalY=0 NormalZ=1 AngleXU=0 Radius=1.905 StartAngle=1.5708 EndAngle=4.71239
    g17: ArcOfCircle CenterX=4.445 CenterY=24.765 CenterZ=0 NormalX=0 NormalY=0 NormalZ=1 AngleXU=0 Radius=1.905 StartAngle=4.71239 EndAngle=7.85398
    g18: LineSegment StartX=-4.445 StartY=22.86 StartZ=0 EndX=4.445 EndY=22.86 EndZ=0
    g19: LineSegment StartX=-4.445 StartY=26.67 StartZ=0 EndX=4.445 EndY=26.67 EndZ=0
    g20: ArcOfCircle CenterX=-16.0007 CenterY=3.30062 CenterZ=0 NormalX=0 NormalY=0 NormalZ=1 AngleXU=0 Radius=1 StartAngle=1.5708 EndAngle=3.14159
    g21: LineSegment StartX=-16.0007 StartY=4.30062 StartZ=0 EndX=15.9993 EndY=4.30062 EndZ=0
    g22: ArcOfCircle CenterX=15.9993 CenterY=3.30062 CenterZ=0 NormalX=0 NormalY=0 NormalZ=1 AngleXU=0 Radius=1 StartAngle=0 EndAngle=1.5708
    g23: LineSegment StartX=16.9993 StartY=3.30062 StartZ=0 EndX=16.9993 EndY=-28.6994 EndZ=0
    g24: ArcOfCircle CenterX=15.9993 CenterY=-28.6994 CenterZ=0 NormalX=0 NormalY=0 NormalZ=1 AngleXU=0 Radius=1 StartAngle=4.71239 EndAngle=6.28319
    g25: LineSegment StartX=15.9993 StartY=-29.6994 StartZ=0 EndX=-16.0007 EndY=-29.6994 EndZ=0
    g26: ArcOfCircle CenterX=-16.0007 CenterY=-28.6994 CenterZ=0 NormalX=0 NormalY=0 NormalZ=1 AngleXU=0 Radius=1 StartAngle=3.14159 EndAngle=4.71239
    g27: LineSegment StartX=-17.0007 StartY=-28.6994 StartZ=0 EndX=-17.0007 EndY=3.30062 EndZ=0
    g28: GeomPoint [constr] X=-17.0007 Y=4.30062 Z=0
    g29: GeomPoint [constr] X=16.9993 Y=-29.6994 Z=0
    g30: ArcOfCircle CenterX=17.023 CenterY=16.01 CenterZ=0 NormalX=0 NormalY=0 NormalZ=1 AngleXU=0 Radius=1 StartAngle=1.5708 EndAngle=3.14159
    g31: LineSegment StartX=17.023 StartY=17.01 StartZ=0 EndX=21.023 EndY=17.01 EndZ=0
    g32: ArcOfCircle CenterX=21.023 CenterY=16.01 CenterZ=0 NormalX=0 NormalY=0 NormalZ=1 AngleXU=0 Radius=1 StartAngle=8e-16 EndAngle=1.5708
    g33: LineSegment StartX=22.023 StartY=16.01 StartZ=0 EndX=22.023 EndY=9.39 EndZ=0
    g34: ArcOfCircle CenterX=21.023 CenterY=9.39 CenterZ=0 NormalX=0 NormalY=0 NormalZ=1 AngleXU=0 Radius=1 StartAngle=4.71239 EndAngle=6.28319
    g35: LineSegment StartX=21.023 StartY=8.39 StartZ=0 EndX=17.023 EndY=8.39 EndZ=0
    g36: ArcOfCircle CenterX=17.023 CenterY=9.39 CenterZ=0 NormalX=0 NormalY=0 NormalZ=1 AngleXU=0 Radius=1 StartAngle=3.14159 EndAngle=4.71239
    g37: LineSegment StartX=16.023 StartY=9.39 StartZ=0 EndX=16.023 EndY=16.01 EndZ=0
    g38: GeomPoint [constr] X=16.023 Y=17.01 Z=0
    g39: GeomPoint [constr] X=22.023 Y=8.39 Z=0
    g40: Circle CenterX=-25.4 CenterY=-25.4 CenterZ=0 NormalX=0 NormalY=0 NormalZ=1 AngleXU=0 Radius=1.525
    g41: Circle CenterX=25.4 CenterY=-25.4 CenterZ=0 NormalX=0 NormalY=0 NormalZ=1 AngleXU=0 Radius=1.525
  constraints (88):
    c: Horizontal(g0)
    c: Horizontal(g2)
    c: Vertical(g1)
    c: PointOnObject(g5,g0)
    c: PointOnObject(g5,g3)
    c: Tangent(g0,g4) = 1.5708
    c: Tangent(g3,g4) = 1.5708
    c: PointOnObject(g7,g0)
    c: PointOnObject(g7,g1)
    c: Tangent(g0,g6) = 1.5708
    c: Tangent(g1,g6) = 1.5708
    c: PointOnObject(g9,g1)
    c: PointOnObject(g9,g2)
    c: Tangent(g1,g8) = 1.5708
    c: Tangent(g2,g8) = 1.5708
    c: PointOnObject(g11,g2)
    c: PointOnObject(g11,g3)
    c: Tangent(g2,g10) = 1.5708
    c: Tangent(g3,g10) = 1.5708
    c: Coincident(g12,g10)
    c: Coincident(g13,g8)
    c: Coincident(g14,g6)
    c: Coincident(g15,g4)
    c: Equal(g15,g14)
    c: Equal(g14,g13)
    c: Equal(g13,g12)
    c: Tangent(g16,g19) = 1.5708
    c: Tangent(g16,g18) = -1.5708
    c: Tangent(g18,g17) = -1.5708
    c: Tangent(g19,g17) = 1.5708
    c: Horizontal(g18)
    c: Diameter(g15) = 3.05
    c: Tangent(g20,g21) = 1.5708
    c: Tangent(g21,g22) = 1.5708
    c: Tangent(g22,g23) = 1.5708
    c: Tangent(g23,g24) = 1.5708
    c: Tangent(g24,g25) = 1.5708
    c: Tangent(g25,g26) = 1.5708
    c: Tangent(g26,g27) = 1.5708
    c: Tangent(g27,g20) = 1.5708
    c: Horizontal(g21)
    c: Horizontal(g25)
    c: Vertical(g23)
    c: Vertical(g27)
    c: Equal(g20,g22)
    c: Equal(g22,g24)
    c: Equal(g24,g26)
    c: PointOnObject(g28,g21)
    c: PointOnObject(g28,g27)
    c: PointOnObject(g29,g23)
    c: PointOnObject(g29,g25)
    c: DistanceY(g20,g20) = 1
    c: Tangent(g30,g31) = 1.5708
    c: Tangent(g31,g32) = 1.5708
    c: Tangent(g32,g33) = 1.5708
    c: Tangent(g33,g34) = 1.5708
    c: Tangent(g34,g35) = 1.5708
    c: Tangent(g35,g36) = 1.5708
    c: Tangent(g36,g37) = 1.5708
    c: Tangent(g37,g30) = 1.5708
    c: Horizontal(g31)
    c: Horizontal(g35)
    c: Vertical(g33)
    c: Vertical(g37)
    c: Equal(g30,g32)
    c: Equal(g32,g34)
    c: Equal(g34,g36)
    c: PointOnObject(g38,g31)
    c: PointOnObject(g38,g37)
    c: PointOnObject(g39,g33)
    c: PointOnObject(g39,g35)
    c: DistanceY(g30,g30) = 1
    c: Equal(g41,g40)
    c: Equal(g40,g15)
    c: Coincident(g10,g-3)
    c: Equal(g10,g-4)
    c: Coincident(g8,g-5)
    c: Coincident(g6,g-6)
    c: Coincident(g4,g-7)
    c: Coincident(g16,g-8)
    c: Coincident(g17,g-9)
    c: Equal(g-8,g16)
    c: Coincident(g41,g-10)
    c: Coincident(g40,g-11)
    c: Coincident(g24,g-13)
    c: Coincident(g20,g-12)
    c: Coincident(g34,g-15)
    c: Coincident(g30,g-14)
FEATURE [PartDesign::Pad] Pad003
  AddSubType = 0
  AutoTaperInnerAngle = false
  CheckUpToFaceLimits = true
  ClaimChildren = false
  Direction = (0,0,1)
  Fit = 0
  FitJoin = 0
  InnerFit = 0
  InnerFitJoin = 0
  InvalidShape = false
  Length = 3
  Length2 = 100
  NewSolid = false
  Profile = -> Sketch003
  Suppress = false
  TaperInnerAngle = 0
  TaperInnerAngleRev = 0
  TreeRank = 0
  Type = 0
  ValidateShape = true
  _ProfileBasedVersion = 0
FEATURE [PartDesign::Body] Body003  label="Plate_top"
  AutoGroupSolids = false
  ClaimAllChildren = false
  ExportMode = 0
  Group = -> [Sketch003,Pad003,Binder003,Binder005,Binder006,Binder007]
  InvalidShape = false
  Origin = -> Origin013
  Placement = pos=(0,0,0.6) rot=(0,0,1;0rad)
  Tip = -> Pad003
  TreeRank = 0
  ValidateShape = false
  _ExportChildren = -> [Pad003,Binder003,Binder005,Binder006,Binder007]
  _GroupVersion = 1
FEATURE [Part::Part2DObjectPython] Shape2DView001  # Draft 2D object (typed FeaturePython)
  AutoUpdate = true
  Base = -> Body003
  Clip = false
  FuseArch = false
  HiddenLines = false
  InPlace = true
  InvalidShape = false
  OnlySolids = false
  Projection = (0,0,1)
  ProjectionMode = 0
  SegmentLength = 0.05
  Tessellation = false
  TreeRank = 552
  ValidateShape = false
  VisibleOnly = false
FEATURE [PartDesign::SubShapeBinder] Binder  label="Binder(Pcb_fc76)"
  BindCopyOnChange = 0
  BindMode = 0
  ClaimChildren = false
  Context = -> Group [Body002.Binder.]
  EdgeTolerance = 1e-06
  FillStyle = 0
  FixShape = 1
  Fuse = false
  InvalidShape = false
  MakeFace = true
  MergeEdges = true
  OffsetFill = false
  OffsetIntersection = false
  OffsetJoinType = 0
  OffsetOpenResult = false
  Outline = false
  PartialLoad = false
  Relative = true
  SplitEdges = false
  Support = -> [Board_fc76[Board_Geoms_fc76.Pcb_fc76.]]
  TightBound = false
  TreeRank = 4421
  ValidateShape = false
  _Version = 8
FEATURE [Sketcher::SketchObject] Sketch002
  ArcFitTolerance = 0
  ExternalBSplineMaxDegree = 0
  ExternalBSplineTolerance = 0
  ExternalGeometry = -> [Binder]
  FullyConstrained = true
  InternalTolerance = 1e-06
  InvalidShape = false
  MakeInternals = false
  MapMode = 5
  Placement = pos=(0,0,-1.6) rot=(1,0,0;3.14159rad)
  TreeRank = 0
  ValidateShape = false
  sketch-geometry (2):
    g0: Circle CenterX=-25.4 CenterY=-25.4 CenterZ=0 NormalX=0 NormalY=0 NormalZ=1 AngleXU=0 Radius=1.525
    g1: Circle CenterX=-25.4 CenterY=-25.4 CenterZ=0 NormalX=0 NormalY=0 NormalZ=1 AngleXU=0 Radius=3
  constraints (6):
    c: Coincident(g1,g0)
    c: Diameter(g0) = 3.05
    c: Diameter(g1) = 6
    c: Coincident(g0,g-3)
    c: DistanceX(g0,g-4) = 50.8  'spacer_x_dim'
    c: DistanceY(g-4,g-5) = 50.8  'spacer_y_dim'
FEATURE [PartDesign::Pad] Pad002
  AddSubType = 0
  AutoTaperInnerAngle = false
  CheckUpToFaceLimits = true
  ClaimChildren = false
  Direction = (0,-1e-16,-1)
  Fit = 0
  FitJoin = 0
  InnerFit = 0
  InnerFitJoin = 0
  InvalidShape = false
  Length = 3
  Length2 = 100
  NewSolid = false
  Profile = -> Sketch002
  Suppress = false
  TaperInnerAngle = 0
  TaperInnerAngleRev = 0
  TreeRank = 0
  Type = 0
  ValidateShape = true
  _ProfileBasedVersion = 0
FEATURE [PartDesign::Body] Body002  label="Spacer_bottom1"
  AutoGroupSolids = false
  ClaimAllChildren = false
  ExportMode = 0
  Group = -> [Sketch002,Pad002,Binder]
  InvalidShape = false
  Origin = -> Origin021
  Tip = -> Pad002
  TreeRank = 0
  ValidateShape = false
  _ExportChildren = -> [Pad002,Binder]
  _GroupVersion = 1
FEATURE [PartDesign::FeatureBase] Clone
  BaseFeature = -> Body002
  InvalidShape = false
  NewSolid = false
  Placement = pos=(0,0,4e-16) rot=(0,0,1;0rad)
  Suppress = false
  TreeRank = 0
  ValidateShape = true
FEATURE [PartDesign::Body] Body006  label="Spacer_bottom2"
  AutoGroupSolids = false
  BaseFeature = -> Body002
  ClaimAllChildren = false
  ExportMode = 0
  Group = -> [Clone]
  InvalidShape = false
  Origin = -> Origin022
  Placement = pos=(50.8,0,0) rot=(0,0,1;0rad)
  Tip = -> Clone
  TreeRank = 0
  ValidateShape = false
  _ExportChildren = -> [Clone]
  _GroupVersion = 1
  expr: Placement.Base.x = Sketch002.Constraints.spacer_x_dim
FEATURE [PartDesign::FeatureBase] Clone001
  BaseFeature = -> Body002
  InvalidShape = false
  NewSolid = false
  Placement = pos=(0,0,4e-16) rot=(0,0,1;0rad)
  Suppress = false
  TreeRank = 0
  ValidateShape = true
FEATURE [PartDesign::Body] Body007  label="Spacer_bottom3"
  AutoGroupSolids = false
  BaseFeature = -> Body002
  ClaimAllChildren = false
  ExportMode = 0
  Group = -> [Clone001]
  InvalidShape = false
  Origin = -> Origin023
  Placement = pos=(50.8,-50.8,0) rot=(0,0,1;0rad)
  Tip = -> Clone001
  TreeRank = 0
  ValidateShape = false
  _ExportChildren = -> [Clone001]
  _GroupVersion = 1
  expr: Placement.Base.x = Sketch002.Constraints.spacer_x_dim
  expr: Placement.Base.y = -Sketch002.Constraints.spacer_y_dim
FEATURE [PartDesign::FeatureBase] Clone002
  BaseFeature = -> Body002
  InvalidShape = false
  NewSolid = false
  Placement = pos=(0,0,4e-16) rot=(0,0,1;0rad)
  Suppress = false
  TreeRank = 0
  ValidateShape = true
FEATURE [PartDesign::Body] Body008  label="Spacer_bottom4"
  AutoGroupSolids = false
  BaseFeature = -> Body002
  ClaimAllChildren = false
  ExportMode = 0
  Group = -> [Clone002]
  InvalidShape = false
  Origin = -> Origin024
  Placement = pos=(0,-50.8,0) rot=(0,0,1;0rad)
  Tip = -> Clone002
  TreeRank = 0
  ValidateShape = false
  _ExportChildren = -> [Clone002]
  _GroupVersion = 1
  expr: Placement.Base.y = -Sketch002.Constraints.spacer_y_dim
FEATURE [App::DocumentObjectGroup] Group  label="Bottom_Spacers"
  ClaimAllChildren = true
  ExportMode = 1
  Group = -> [Body002,Body006,Body007,Body008]
  TreeRank = 0
  _GroupVersion = 1
FEATURE [Part::Part2DObjectPython] Shape2DView003  # Draft 2D object (typed FeaturePython)
  AutoUpdate = true
  Base = -> Body002
  Clip = false
  FixShape = 1
  FuseArch = false
  HiddenLines = false
  InPlace = true
  InvalidShape = false
  OnlySolids = false
  Projection = (0,0,1)
  ProjectionMode = 0
  SegmentLength = 0.05
  Tessellation = false
  TreeRank = 4426
  ValidateShape = false
  VisibleOnly = false
FEATURE [App::DocumentObjectGroup] Group002  label="DXF"
  ClaimAllChildren = true
  ExportMode = 1
  Group = -> [Shape2DView,Shape2DView001,Shape2DView003]
  TreeRank = 554
  _GroupVersion = 1
